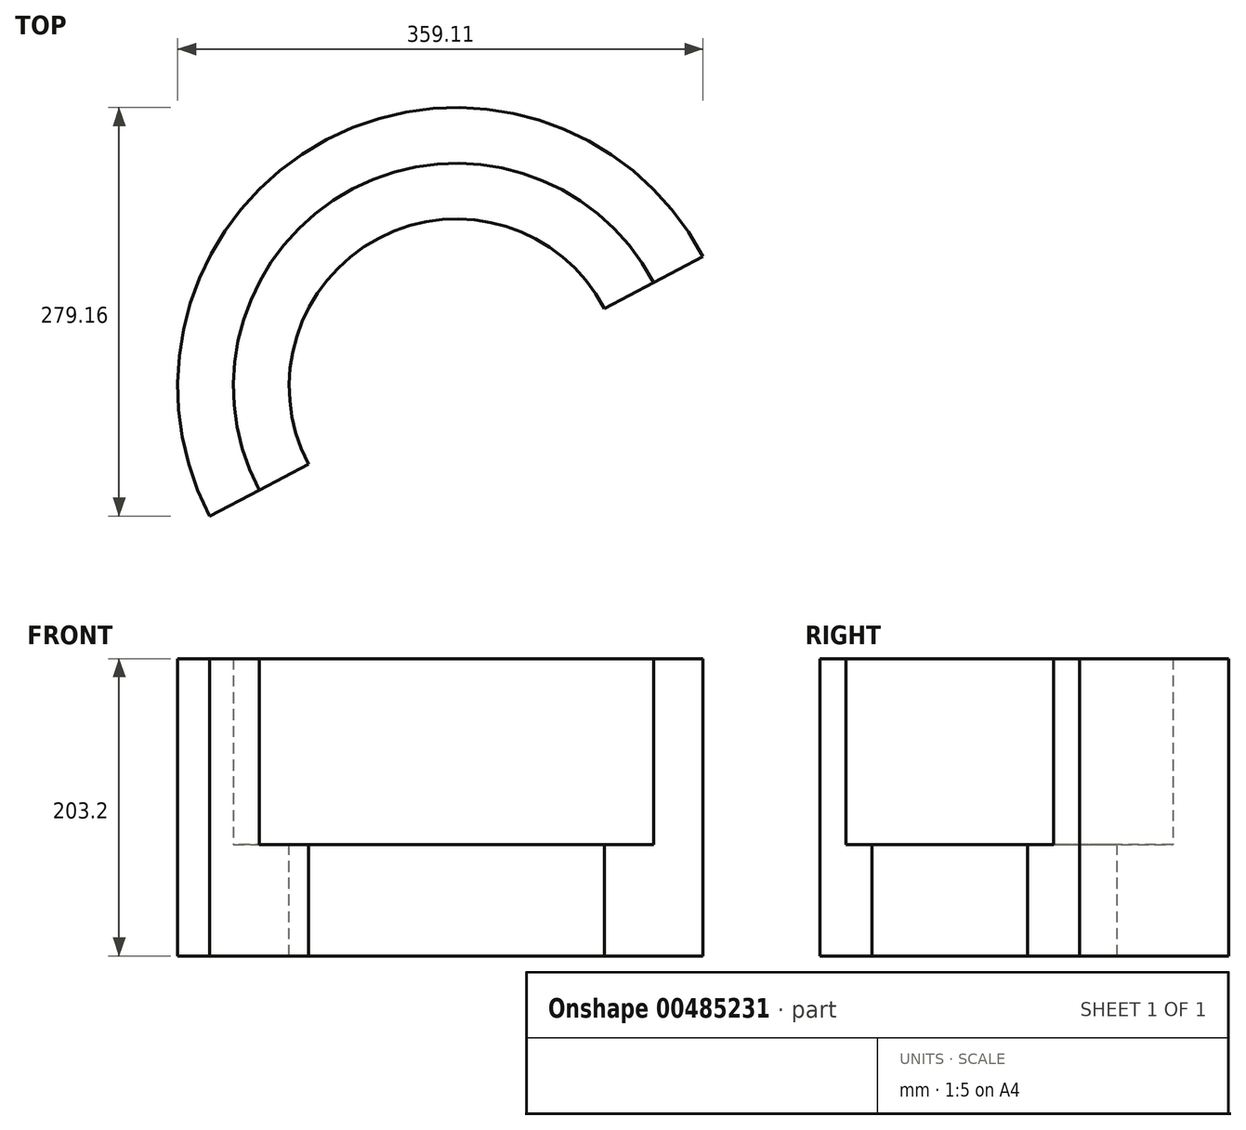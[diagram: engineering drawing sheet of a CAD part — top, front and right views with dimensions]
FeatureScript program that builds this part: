
annotation { "Feature Type Name" : "Feature", "Feature Type Description" : "" }
export const myFeature = defineFeature(function(context is Context, id is Id, definition is map)
    precondition{}
    {
        {
            var Q0;
            Q0=qCreatedBy(makeId("Top.planeOp"),FACE);
            var sketch = newSketch(context, id + "F0", { "sketchPlane" : qUnion([Q0])});
            skArc(sketch, "E0", {"start": v(134.89, 70.93) * mm, "mid": v(-70.93, 134.89) * mm, "end": v(-134.89, -70.93) * mm});
            skArc(sketch, "E1", {"start": v(101.17, 53.2) * mm, "mid": v(-53.2, 101.17) * mm, "end": v(-101.17, -53.2) * mm});
            skArc(sketch, "E2", {"start": v(168.6, 88.66) * mm, "mid": v(-88.66, 168.6) * mm, "end": v(-168.6, -88.66) * mm});
            skLineSegment(sketch, "E3", {"start": v(168.6, 88.66) * mm, "end": v(101.17, 53.2) * mm});
            skLineSegment(sketch, "E4", {"start": v(-101.17, -53.2) * mm, "end": v(-168.6, -88.66) * mm});
            skSolve(sketch);
        }
        {
            var Q0;
            {var subQ0=sQuery(id+"F0.wireOp",EDGE,"E0");Q0=makeQuery(id+"F0.imprint","IMPRINT",FACE,{"disambiguationData":[TD([[makeQuery(id+"F0.imprint","IMPRINT",EDGE,{"derivedFrom":subQ0}),-1.0]])]});}
            extrude(context, id + "F1", {"entities" : qUnion([Q0]), "depth" : 127 * mm});
        }
        {
            var Q0;
            Q0=makeQuery(id+"F1.opExtrude","CAP_FACE",FACE,{"disambiguationData":[OSD([sQuery(id+"F0.wireOp",EDGE,"E0"),sQuery(id+"F0.wireOp",EDGE,"E2"),sQuery(id+"F0.wireOp",EDGE,"E3"),sQuery(id+"F0.wireOp",EDGE,"E4")])],"isStart":true});
            var sketch = newSketch(context, id + "F2", { "sketchPlane" : qUnion([Q0])});
            skArc(sketch, "E5", {"start": v(-168.6, 88.66) * mm, "mid": v(-88.66, -168.6) * mm, "end": v(168.6, -88.66) * mm});
            skArc(sketch, "E6", {"start": v(-101.17, 53.2) * mm, "mid": v(-53.2, -101.17) * mm, "end": v(101.17, -53.2) * mm});
            skLineSegment(sketch, "E7", {"start": v(-168.6, 88.66) * mm, "end": v(-101.17, 53.2) * mm});
            skLineSegment(sketch, "E8.trimOffspring", {"start": v(101.17, -53.2) * mm, "end": v(168.6, -88.66) * mm});
            skSolve(sketch);
        }
        {
            var Q0;
            Q0 = qSketchRegion(id + "F2", true);
            extrude(context, id + "F3", {"entities" : qUnion([Q0]), "operationType" : NewBodyOperationType.ADD, "depth" : 76.2 * mm});
        }
    });
